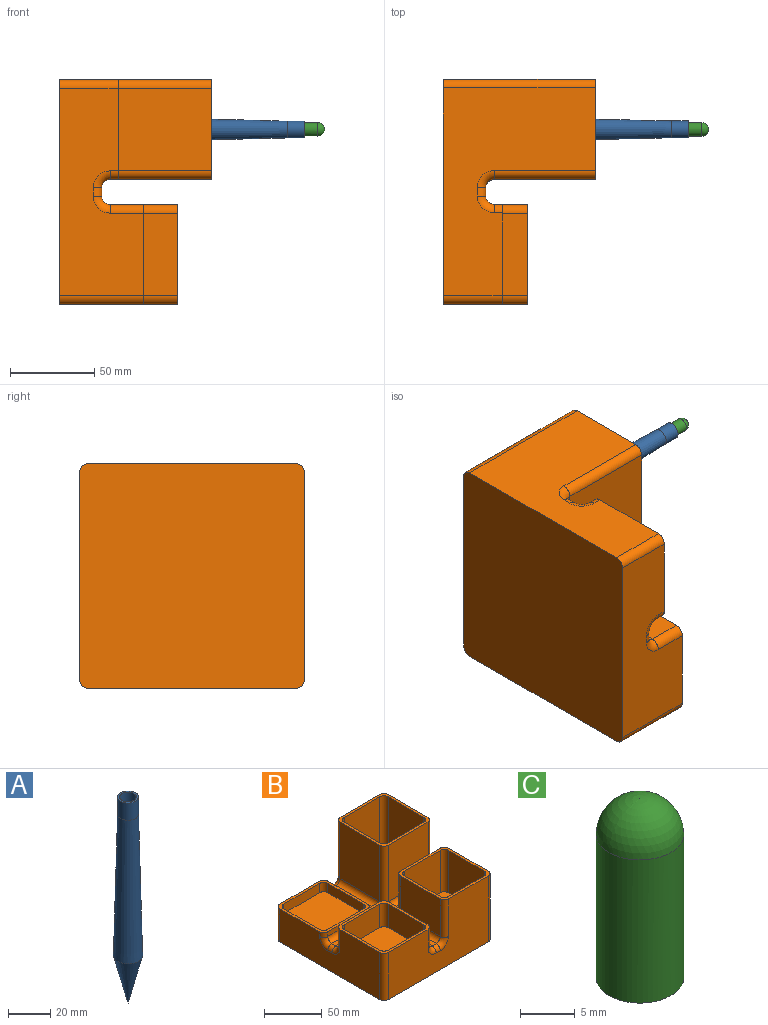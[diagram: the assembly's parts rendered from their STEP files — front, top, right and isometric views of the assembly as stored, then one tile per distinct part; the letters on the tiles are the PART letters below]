
ASSEMBLY  parts=3 mates=2
PART A: 6 faces, bbox 13.9x13.9x120 mm
  f0: cone r=0mm half-angle=14.1deg, axis (0,0,1), area 624.5mm2, adj f1
  f1: cone r=6.95mm half-angle=1.4deg, axis (0,0,-1), area 3089.7mm2, adj f0,f2
  f2: cylinder r=5mm len=10mm, axis (0,0,-1), area 314.2mm2, adj f1,f3
  f3: plane 10x10mm, normal (0,0,1), area 28.3mm2, adj f2,f4
  f4: cylinder r=4mm len=8mm, axis (0,0,1), area 201.1mm2, adj f3,f5
  f5: plane 8x8mm, normal (0,0,1), area 50.3mm2, adj f4
PART B: 94 faces, bbox 133x133x90 mm
  f0: plane 59x59mm, normal (0,0,1), area 565mm2, adj f5,f6,f10,f24,f25,f26,f27,f28
  f1: plane 59x59mm, normal (0,0,1), area 565mm2, adj f6,f7,f11,f29,f30,f31,f32,f33
  f2: plane 59x59mm, normal (0,0,1), area 565mm2, adj f4,f7,f12,f19,f20,f21,f22,f23
  f3: plane 123x123mm, normal (0,0,1), area 1290.8mm2, adj f70,f71,f72,f75,f76,f79,f80,f81
  f4: plane 123x50mm, normal (-1,0,0), area 4707.9mm2, adj f2,f8,f9,f12,f15,f16,f21,f74
  f5: plane 123x70mm, normal (0,-1,0), area 6422.9mm2, adj f0,f8,f9,f10,f15,f17,f28,f73
  f6: plane 123x90mm, normal (1,0,0), area 8382.9mm2, adj f0,f1,f8,f10,f11,f26,f31,f85
  f7: plane 123x90mm, normal (0,1,0), area 6667.9mm2, adj f1,f2,f8,f11,f12,f23,f32,f86
  f8: plane 133x133mm, normal (0,0,-1), area 17667.5mm2, adj f4,f5,f6,f7,f9,f10,f11,f12
  f9: cylinder r=5mm len=50mm, axis (0,0,1), area 392.7mm2, adj f4,f5,f8,f15
  f10: cylinder r=5mm len=70mm, axis (0,0,-1), area 549.8mm2, adj f0,f5,f6,f8
  f11: cylinder r=5mm len=90mm, axis (0,0,1), area 706.9mm2, adj f1,f6,f7,f8
  f12: cylinder r=5mm len=35mm, axis (0,0,-1), area 274.9mm2, adj f2,f4,f7,f8
  f13: plane 49x20mm, normal (1,0,0), area 980mm2, adj f15,f17,f18,f71
  f14: plane 49x20mm, normal (0,1,0), area 980mm2, adj f15,f16,f18,f72
  f15: plane 59x59mm, normal (0,0,1), area 565mm2, adj f4,f5,f9,f13,f14,f16,f17,f18
  f16: cylinder r=5mm len=20mm, axis (0,0,-1), area 157.1mm2, adj f4,f14,f15,f74
  f17: cylinder r=5mm len=20mm, axis (0,0,-1), area 157.1mm2, adj f5,f13,f15,f73
  f18: cylinder r=5mm len=20mm, axis (0,0,1), area 157.1mm2, adj f13,f14,f15,f70
  f19: plane 49x5mm, normal (0,-1,0), area 245mm2, adj f2,f21,f22,f80
  f20: plane 49x5mm, normal (1,0,0), area 245mm2, adj f2,f22,f23,f84
  f21: cylinder r=5mm len=5mm, axis (0,0,1), area 39.3mm2, adj f2,f4,f19,f78
  f22: cylinder r=5mm len=5mm, axis (0,0,1), area 39.3mm2, adj f2,f19,f20,f82
  f23: cylinder r=5mm len=5mm, axis (0,0,-1), area 39.3mm2, adj f2,f7,f20,f86
  f24: plane 49x40mm, normal (0,1,0), area 1960mm2, adj f0,f26,f27,f83
  f25: plane 49x40mm, normal (-1,0,0), area 1960mm2, adj f0,f27,f28,f79
  f26: cylinder r=5mm len=40mm, axis (0,0,-1), area 314.2mm2, adj f0,f6,f24,f85
  f27: cylinder r=5mm len=40mm, axis (0,0,1), area 314.2mm2, adj f0,f24,f25,f81
  f28: cylinder r=5mm len=40mm, axis (0,0,1), area 314.2mm2, adj f0,f5,f25,f77
  f29: plane 60x49mm, normal (-1,0,0), area 2940mm2, adj f1,f32,f33,f92
  f30: plane 60x49mm, normal (0,-1,0), area 2940mm2, adj f1,f31,f33,f91
  f31: cylinder r=5mm len=60mm, axis (0,0,1), area 471.2mm2, adj f1,f6,f30,f89
  f32: cylinder r=5mm len=60mm, axis (0,0,1), area 471.2mm2, adj f1,f7,f29,f90
  f33: cylinder r=5mm len=60mm, axis (0,0,1), area 471.2mm2, adj f1,f29,f30,f93
  f34: plane 44x25mm, normal (1,0,0), area 1100mm2, adj f15,f35,f41,f42
  f35: cylinder r=5mm len=25mm, axis (0,0,1), area 196.3mm2, adj f15,f34,f36,f42
  f36: plane 44x25mm, normal (0,1,0), area 1100mm2, adj f15,f35,f37,f42
  f37: cylinder r=5mm len=25mm, axis (0,0,1), area 196.3mm2, adj f15,f36,f38,f42
  f38: plane 44x25mm, normal (-1,0,0), area 1100mm2, adj f15,f37,f39,f42
  f39: cylinder r=5mm len=25mm, axis (0,0,1), area 196.3mm2, adj f15,f38,f40,f42
  f40: plane 44x25mm, normal (0,-1,0), area 1100mm2, adj f15,f39,f41,f42
  f41: cylinder r=5mm len=25mm, axis (0,0,1), area 196.3mm2, adj f15,f34,f40,f42
  f42: plane 54x54mm, normal (0,0,1), area 2894.5mm2, adj f34,f35,f36,f37,f38,f39,f40,f41
  f43: plane 44x10mm, normal (-1,0,0), area 440mm2, adj f2,f44,f50,f51
  f44: cylinder r=5mm len=10mm, axis (0,0,1), area 78.5mm2, adj f2,f43,f45,f51
  f45: plane 44x10mm, normal (0,-1,0), area 440mm2, adj f2,f44,f46,f51
  f46: cylinder r=5mm len=10mm, axis (0,0,1), area 78.5mm2, adj f2,f45,f47,f51
  f47: plane 44x10mm, normal (1,0,0), area 440mm2, adj f2,f46,f48,f51
  f48: cylinder r=5mm len=10mm, axis (0,0,1), area 78.5mm2, adj f2,f47,f49,f51
  f49: plane 44x10mm, normal (0,1,0), area 440mm2, adj f2,f48,f50,f51
  f50: cylinder r=5mm len=10mm, axis (0,0,1), area 78.5mm2, adj f2,f43,f49,f51
  f51: plane 54x54mm, normal (0,0,1), area 2894.5mm2, adj f43,f44,f45,f46,f47,f48,f49,f50
  f52: plane 65x44mm, normal (0,-1,0), area 2860mm2, adj f1,f53,f59,f60
  f53: cylinder r=5mm len=65mm, axis (0,0,1), area 510.5mm2, adj f1,f52,f54,f60
  f54: plane 65x44mm, normal (1,0,0), area 2860mm2, adj f1,f53,f55,f60
  f55: cylinder r=5mm len=65mm, axis (0,0,1), area 510.5mm2, adj f1,f54,f56,f60
  f56: plane 65x44mm, normal (0,1,0), area 2860mm2, adj f1,f55,f57,f60
  f57: cylinder r=5mm len=65mm, axis (0,0,1), area 510.5mm2, adj f1,f56,f58,f60
  f58: plane 65x44mm, normal (-1,0,0), area 2860mm2, adj f1,f57,f59,f60
  f59: cylinder r=5mm len=65mm, axis (0,0,1), area 510.5mm2, adj f1,f52,f58,f60
  f60: plane 54x54mm, normal (0,0,1), area 2894.5mm2, adj f52,f53,f54,f55,f56,f57,f58,f59
  f61: plane 45x44mm, normal (0,-1,0), area 1980mm2, adj f0,f62,f68,f69
  f62: cylinder r=5mm len=45mm, axis (0,0,1), area 353.4mm2, adj f0,f61,f63,f69
  f63: plane 45x44mm, normal (1,0,0), area 1980mm2, adj f0,f62,f64,f69
  f64: cylinder r=5mm len=45mm, axis (0,0,1), area 353.4mm2, adj f0,f63,f65,f69
  f65: plane 45x44mm, normal (0,1,0), area 1980mm2, adj f0,f64,f66,f69
  f66: cylinder r=5mm len=45mm, axis (0,0,1), area 353.4mm2, adj f0,f65,f67,f69
  f67: plane 45x44mm, normal (-1,0,0), area 1980mm2, adj f0,f66,f68,f69
  f68: cylinder r=5mm len=45mm, axis (0,0,1), area 353.4mm2, adj f0,f61,f67,f69
  f69: plane 54x54mm, normal (0,0,1), area 2894.5mm2, adj f61,f62,f63,f64,f65,f66,f67,f68
  f70: torus R=10mm, axis (0,0,1), area 84.1mm2, adj f3,f18,f71,f72
  f71: cylinder r=5mm len=49mm, axis (0,1,0), area 384.8mm2, adj f3,f13,f70,f73
  f72: cylinder r=5mm len=49mm, axis (-1,0,0), area 384.8mm2, adj f3,f14,f70,f74
  f73: torus R=10mm, axis (0,1,0), area 84.1mm2, adj f5,f17,f71,f75
  f74: torus R=10mm, axis (-1,0,0), area 84.1mm2, adj f4,f16,f72,f76
  f75: cylinder r=5mm len=5mm, axis (-1,0,0), area 39.3mm2, adj f3,f5,f73,f77
  f76: cylinder r=5mm len=5mm, axis (0,1,0), area 39.3mm2, adj f3,f4,f74,f78
  f77: torus R=10mm, axis (0,1,0), area 84.1mm2, adj f5,f28,f75,f79
  f78: torus R=10mm, axis (-1,0,0), area 84.1mm2, adj f4,f21,f76,f80
  f79: cylinder r=5mm len=49mm, axis (0,-1,0), area 384.8mm2, adj f3,f25,f77,f81
  f80: cylinder r=5mm len=49mm, axis (1,0,0), area 384.8mm2, adj f3,f19,f78,f82
  f81: torus R=10mm, axis (0,0,1), area 84.1mm2, adj f3,f27,f79,f83
  f82: torus R=10mm, axis (0,0,1), area 84.1mm2, adj f3,f22,f80,f84
  f83: cylinder r=5mm len=49mm, axis (-1,0,0), area 384.8mm2, adj f3,f24,f81,f85
  f84: cylinder r=5mm len=49mm, axis (0,1,0), area 384.8mm2, adj f3,f20,f82,f86
  f85: torus R=10mm, axis (-1,0,0), area 84.1mm2, adj f6,f26,f83,f87
  f86: torus R=10mm, axis (0,1,0), area 84.1mm2, adj f7,f23,f84,f88
  f87: cylinder r=5mm len=5mm, axis (0,-1,0), area 39.3mm2, adj f3,f6,f85,f89
  f88: cylinder r=5mm len=5mm, axis (1,0,0), area 39.3mm2, adj f3,f7,f86,f90
  f89: torus R=10mm, axis (-1,0,0), area 84.1mm2, adj f6,f31,f87,f91
  f90: torus R=10mm, axis (0,1,0), area 84.1mm2, adj f7,f32,f88,f92
  f91: cylinder r=5mm len=49mm, axis (1,0,0), area 384.8mm2, adj f3,f30,f89,f93
  f92: cylinder r=5mm len=49mm, axis (0,-1,0), area 384.8mm2, adj f3,f29,f90,f93
  f93: torus R=10mm, axis (0,0,1), area 84.1mm2, adj f3,f33,f91,f92
PART C: 3 faces, bbox 8x8x20 mm
  f0: cylinder r=4mm len=16mm, axis (0,0,-1), area 402.1mm2, adj f1,f2
  f1: plane 8x8mm, normal (0,0,-1), area 50.3mm2, adj f0
  f2: sphere r=4mm, area 100.5mm2, adj f0
PLACE A rot(axis=(0,1,0),90deg) t=(-25,103.5,98.5)mm
PLACE B rot(axis=(0.58,0.58,0.58),120deg) t=(-50,0,-5)mm
PLACE C rot(axis=(0,1,0),90deg) t=(87,103.5,98.5)mm
MATE fastened C.f0 <-> A.f4  axis (-1,0,0) through (87,103.5,98.5)mm
MATE fastened A.f0 <-> B.f60  axis (1,0,0) through (-25,103.5,98.5)mm
